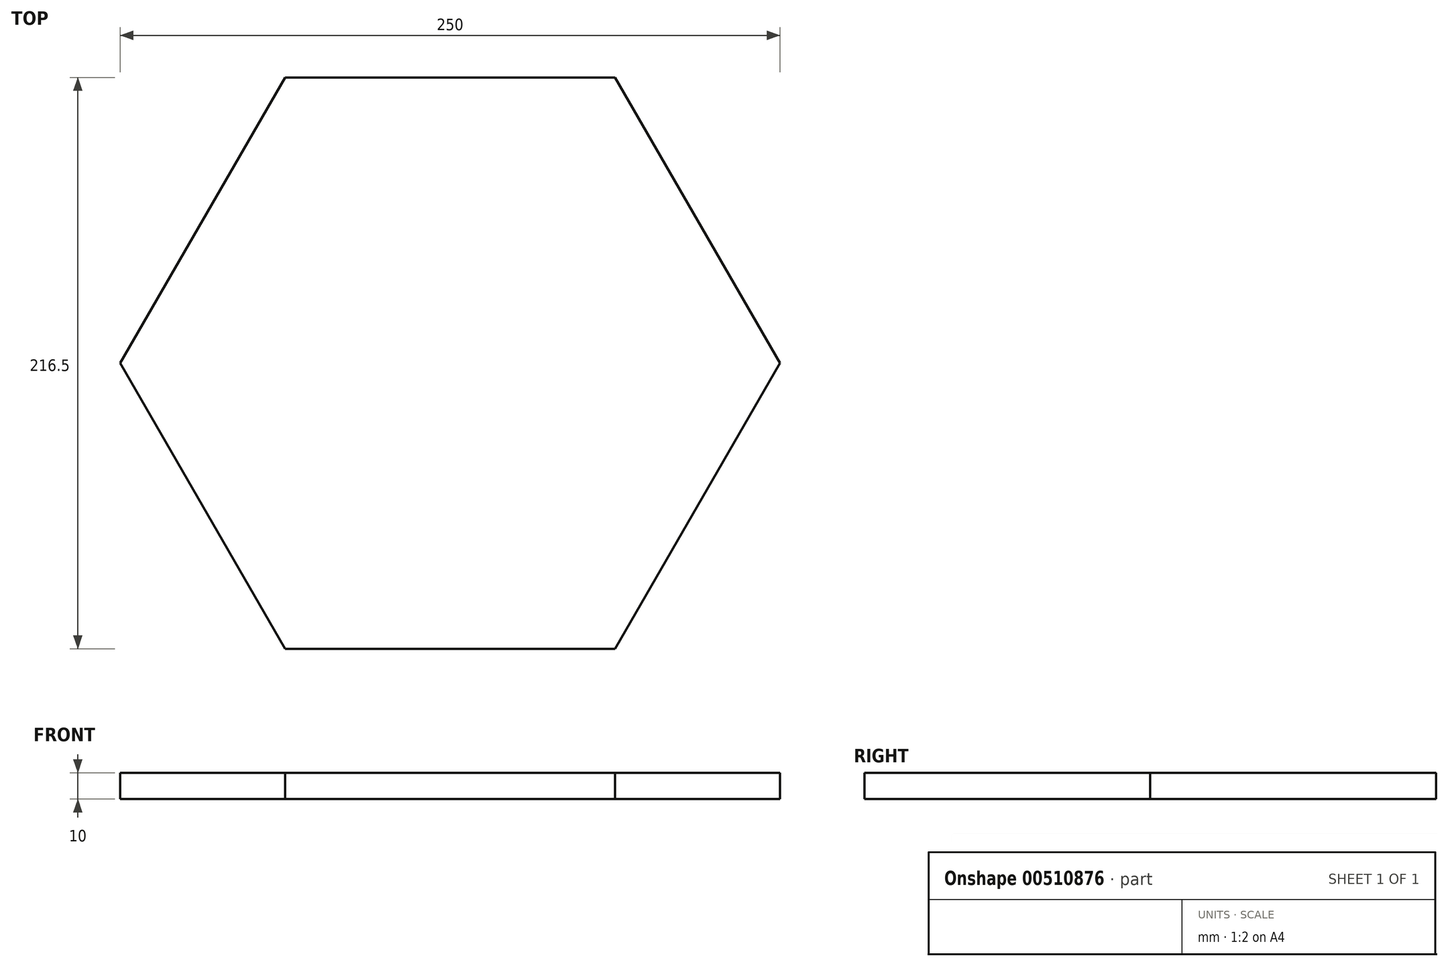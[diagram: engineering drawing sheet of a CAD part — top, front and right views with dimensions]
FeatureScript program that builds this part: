
annotation { "Feature Type Name" : "Feature", "Feature Type Description" : "" }
export const myFeature = defineFeature(function(context is Context, id is Id, definition is map)
    precondition{}
    {
        {
            var Q0;
            Q0=qCreatedBy(makeId("Top.planeOp"),FACE);
            var sketch = newSketch(context, id + "F0", { "sketchPlane" : qUnion([Q0])});
            skCircle(sketch, "E0.cCircle", {"center": v(0, 0) * mm, "radius": 108.25 * mm, "construction": true});
            skLineSegment(sketch, "E0.0", {"start": v(-62.5, 108.25) * mm, "end": v(62.5, 108.25) * mm});
            skLineSegment(sketch, "E0.1", {"start": v(62.5, 108.25) * mm, "end": v(125, 0) * mm});
            skLineSegment(sketch, "E0.2", {"start": v(125, 0) * mm, "end": v(62.5, -108.25) * mm});
            skLineSegment(sketch, "E0.3", {"start": v(62.5, -108.25) * mm, "end": v(-62.5, -108.25) * mm});
            skLineSegment(sketch, "E0.4", {"start": v(-62.5, -108.25) * mm, "end": v(-125, 0) * mm});
            skLineSegment(sketch, "E0.5", {"start": v(-125, 0) * mm, "end": v(-62.5, 108.25) * mm});
            skPoint(sketch, "E0.0.midPoint", {"position": v(0, 108.25) * mm});
            skSolve(sketch);
        }
        {
            var Q0;
            Q0=makeQuery(id+"F0.imprint","IMPRINT",FACE,{"disambiguationData":[TD([[makeQuery(id+"F0.imprint","IMPRINT",EDGE,{"derivedFrom":sQuery(id+"F0.wireOp",EDGE,"E0.0")}),-1.0]])]});
            extrude(context, id + "F1", {"entities" : qUnion([Q0]), "flatOperationType" : FlatOperationType.REMOVE, "offsetDistance" : 25 * mm, "depth" : 10 * mm, "domain" : OperationDomain.MODEL});
        }
    });
